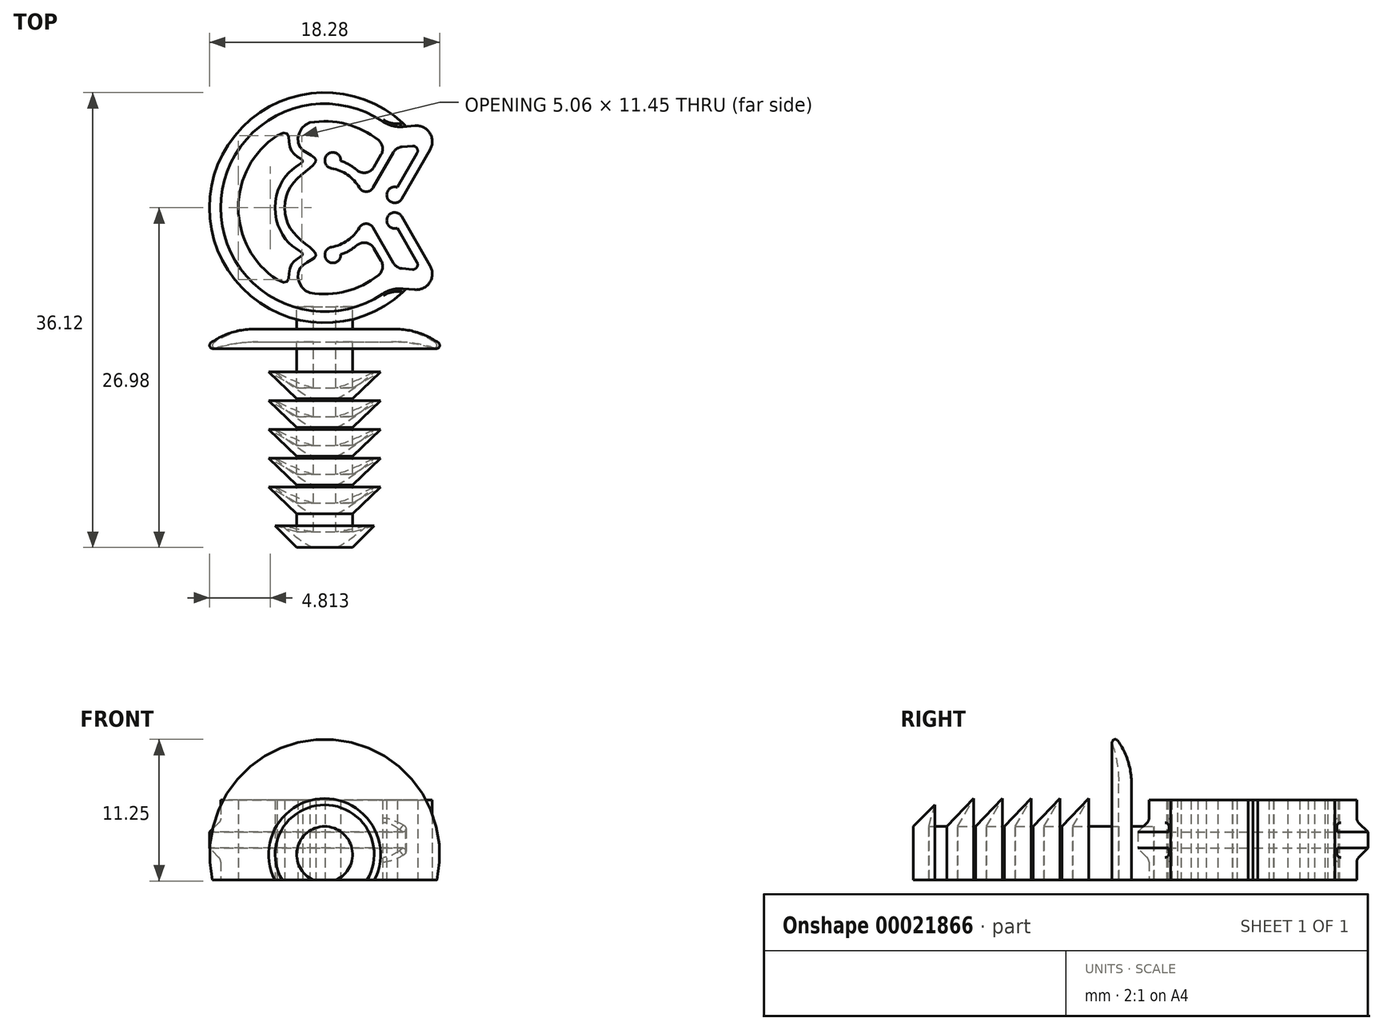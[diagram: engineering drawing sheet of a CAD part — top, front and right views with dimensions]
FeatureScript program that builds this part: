
annotation { "Feature Type Name" : "Feature", "Feature Type Description" : "" }
export const myFeature = defineFeature(function(context is Context, id is Id, definition is map)
    precondition{}
    {
        {
            var Q0;
            Q0=qCreatedBy(makeId("Top.planeOp"),FACE);
            var sketch = newSketch(context, id + "F0", { "sketchPlane" : qUnion([Q0])});
            skLineSegment(sketch, "E0", {"start": v(0, 0) * mm, "end": v(27.93, 0) * mm, "construction": true});
            skLineSegment(sketch, "E1", {"start": v(6.24, 6.43) * mm, "end": v(7.17, 6.52) * mm});
            skLineSegment(sketch, "E2", {"start": v(8.38, 4.62) * mm, "end": v(6.12, 0.7) * mm});
            skLineSegment(sketch, "E3", {"start": v(5.77, 1.62) * mm, "end": v(7.34, 4.34) * mm});
            skLineSegment(sketch, "E4", {"start": v(6.98, 4.9) * mm, "end": v(6.16, 4.83) * mm});
            skArc(sketch, "E5", {"start": v(5.77, 1.62) * mm, "mid": v(4.98, 0.8) * mm, "end": v(6.12, 0.7) * mm});
            skPoint(sketch, "E6.visualSharp", {"position": v(9.6, 6.73) * mm});
            skArc(sketch, "E6.filletArc", {"start": v(8.38, 4.62) * mm, "mid": v(8.35, 5.93) * mm, "end": v(7.17, 6.52) * mm});
            skPoint(sketch, "E7.visualSharp", {"position": v(7.7, 4.97) * mm});
            skArc(sketch, "E7.filletArc", {"start": v(7.34, 4.34) * mm, "mid": v(7.33, 4.73) * mm, "end": v(6.98, 4.9) * mm});
            skArc(sketch, "E8", {"start": v(4.6, 6.86) * mm, "mid": v(-3.88, 7.28) * mm, "end": v(-8.26, 0) * mm});
            skArc(sketch, "E9", {"start": v(4.28, 5.36) * mm, "mid": v(1.7, 6.64) * mm, "end": v(-1.17, 6.76) * mm});
            skLineSegment(sketch, "E10", {"start": v(0, 0) * mm, "end": v(-13.62, 0) * mm, "construction": true});
            skPoint(sketch, "E11.visualSharp", {"position": v(5.27, 6.35) * mm});
            skArc(sketch, "E11.filletArc", {"start": v(4.6, 6.86) * mm, "mid": v(5.38, 6.5) * mm, "end": v(6.24, 6.43) * mm});
            skLineSegment(sketch, "E12", {"start": v(5.47, 4.4) * mm, "end": v(3.85, 1.59) * mm});
            skLineSegment(sketch, "E13", {"start": v(4.5, 4.22) * mm, "end": v(3.91, 3.22) * mm});
            skPoint(sketch, "E14", {"position": v(-0.35, 3.16) * mm});
            skArc(sketch, "E15", {"start": v(2.75, 1.59) * mm, "mid": v(1.82, 2.6) * mm, "end": v(0.54, 3.13) * mm});
            skPoint(sketch, "E16", {"position": v(0.3, 3.88) * mm});
            skPoint(sketch, "E17.visualSharp", {"position": v(3.15, 0.38) * mm});
            skArc(sketch, "E17.filletArc", {"start": v(2.75, 1.59) * mm, "mid": v(3.3, 1.27) * mm, "end": v(3.85, 1.59) * mm});
            skArc(sketch, "E18", {"start": v(1.29, 3.72) * mm, "mid": v(0.26, 4.25) * mm, "end": v(0.54, 3.13) * mm});
            skPoint(sketch, "E19.visualSharp", {"position": v(4.85, 4.85) * mm});
            skArc(sketch, "E19.filletArc", {"start": v(4.5, 4.22) * mm, "mid": v(4.6, 4.83) * mm, "end": v(4.28, 5.36) * mm});
            skPoint(sketch, "E20.visualSharp", {"position": v(5.7, 4.8) * mm});
            skArc(sketch, "E20.filletArc", {"start": v(6.16, 4.83) * mm, "mid": v(5.76, 4.7) * mm, "end": v(5.47, 4.4) * mm});
            skCircle(sketch, "E21", {"center": v(0, 0) * mm, "radius": 3.18 * mm, "construction": true});
            skArc(sketch, "E22", {"start": v(2.56, 2.99) * mm, "mid": v(1.96, 3.42) * mm, "end": v(1.29, 3.72) * mm});
            skLineSegment(sketch, "E23", {"start": v(0, 0) * mm, "end": v(1.94, 4.22) * mm, "construction": true});
            skPoint(sketch, "E24", {"position": v(1.64, 3.58) * mm});
            skPoint(sketch, "E25", {"position": v(1.33, 2.89) * mm});
            skPoint(sketch, "E26.visualSharp", {"position": v(3.3, 2.15) * mm});
            skArc(sketch, "E26.filletArc", {"start": v(2.56, 2.99) * mm, "mid": v(3.3, 2.79) * mm, "end": v(3.91, 3.22) * mm});
            skFitSpline(sketch, "E27", {"points": [v(-1.17, 6.76) * mm, v(-2.03, 4.92) * mm, v(-0.7, 3.83) * mm, v(-2, 2.46) * mm, v(-3.18, 0) * mm], "startDerivative": vector(-8.5, -2.05) * mm, "endDerivative": vector(0.11, -11.22) * mm});
            skFitSpline(sketch, "E28", {"points": [v(-3.78, 5.72) * mm, v(-2.74, 4.77) * mm, v(-1.76, 3.72) * mm, v(-2.58, 3.03) * mm, v(-3.94, 0) * mm], "startDerivative": vector(15.56, 9.08) * mm, "endDerivative": vector(0.12, -11.3) * mm});
            skArc(sketch, "E29.trimOffspring", {"start": v(-3.78, 5.72) * mm, "mid": v(-6.04, 3.25) * mm, "end": v(-6.86, 0) * mm});
            skArc(sketch, "E30.MirrorCS", {"start": v(6.16, -4.83) * mm, "mid": v(5.76, -4.7) * mm, "end": v(5.47, -4.4) * mm});
            skArc(sketch, "E31.MirrorCS", {"start": v(4.5, -4.22) * mm, "mid": v(4.6, -4.83) * mm, "end": v(4.28, -5.36) * mm});
            skPoint(sketch, "E32.MirrorP", {"position": v(5.7, -4.8) * mm});
            skArc(sketch, "E33.MirrorCS", {"start": v(2.56, -2.99) * mm, "mid": v(1.96, -3.42) * mm, "end": v(1.29, -3.72) * mm});
            skArc(sketch, "E34.MirrorCS", {"start": v(2.56, -2.99) * mm, "mid": v(3.3, -2.79) * mm, "end": v(3.91, -3.22) * mm});
            skFitSpline(sketch, "E35.MirrorCS", {"points": [v(-1.17, -6.76) * mm, v(-2.03, -4.92) * mm, v(-0.7, -3.83) * mm, v(-2, -2.46) * mm, v(-3.18, 0) * mm], "startDerivative": vector(-8.5, 2.05) * mm, "endDerivative": vector(0.11, 11.22) * mm});
            skArc(sketch, "E36.MirrorCS", {"start": v(-3.78, -5.72) * mm, "mid": v(-6.04, -3.25) * mm, "end": v(-6.86, 0) * mm});
            skFitSpline(sketch, "E37.MirrorCS", {"points": [v(-3.78, -5.72) * mm, v(-2.74, -4.77) * mm, v(-1.76, -3.72) * mm, v(-2.58, -3.03) * mm, v(-3.94, 0) * mm], "startDerivative": vector(15.56, -9.08) * mm, "endDerivative": vector(0.12, 11.3) * mm});
            skPoint(sketch, "E38.MirrorP", {"position": v(4.85, -4.85) * mm});
            skLineSegment(sketch, "E39.MirrorCS", {"start": v(4.5, -4.22) * mm, "end": v(3.91, -3.22) * mm});
            skLineSegment(sketch, "E40.MirrorCS", {"start": v(5.77, -1.62) * mm, "end": v(7.34, -4.34) * mm});
            skPoint(sketch, "E41.MirrorP", {"position": v(0.3, -3.88) * mm});
            skArc(sketch, "E42.MirrorCS", {"start": v(5.77, -1.62) * mm, "mid": v(4.98, -0.8) * mm, "end": v(6.12, -0.7) * mm});
            skArc(sketch, "E43.MirrorCS", {"start": v(2.75, -1.59) * mm, "mid": v(1.82, -2.6) * mm, "end": v(0.54, -3.13) * mm});
            skLineSegment(sketch, "E44.MirrorCS", {"start": v(6.98, -4.9) * mm, "end": v(6.16, -4.83) * mm});
            skLineSegment(sketch, "E45.MirrorCS", {"start": v(8.38, -4.62) * mm, "end": v(6.12, -0.7) * mm});
            skPoint(sketch, "E46.MirrorP", {"position": v(1.64, -3.58) * mm});
            skLineSegment(sketch, "E47.MirrorCS", {"start": v(6.24, -6.43) * mm, "end": v(7.17, -6.52) * mm});
            skLineSegment(sketch, "E48.MirrorCS", {"start": v(5.47, -4.4) * mm, "end": v(3.85, -1.59) * mm});
            skArc(sketch, "E49.MirrorCS", {"start": v(4.6, -6.86) * mm, "mid": v(5.38, -6.5) * mm, "end": v(6.24, -6.43) * mm});
            skPoint(sketch, "E50.MirrorP", {"position": v(1.33, -2.89) * mm});
            skArc(sketch, "E51.MirrorCS", {"start": v(2.75, -1.59) * mm, "mid": v(3.3, -1.27) * mm, "end": v(3.85, -1.59) * mm});
            skPoint(sketch, "E52.MirrorP", {"position": v(-0.35, -3.16) * mm});
            skPoint(sketch, "E53.MirrorP", {"position": v(5.27, -6.35) * mm});
            skArc(sketch, "E54.MirrorCS", {"start": v(4.28, -5.36) * mm, "mid": v(1.7, -6.64) * mm, "end": v(-1.17, -6.76) * mm});
            skPoint(sketch, "E55.MirrorP", {"position": v(3.15, -0.38) * mm});
            skArc(sketch, "E56.MirrorCS", {"start": v(8.38, -4.62) * mm, "mid": v(8.35, -5.93) * mm, "end": v(7.17, -6.52) * mm});
            skArc(sketch, "E57.MirrorCS", {"start": v(4.6, -6.86) * mm, "mid": v(-3.88, -7.28) * mm, "end": v(-8.26, 0) * mm});
            skPoint(sketch, "E58.MirrorP", {"position": v(3.3, -2.15) * mm});
            skPoint(sketch, "E59.MirrorP", {"position": v(7.7, -4.97) * mm});
            skArc(sketch, "E60.MirrorCS", {"start": v(1.29, -3.72) * mm, "mid": v(0.26, -4.25) * mm, "end": v(0.54, -3.13) * mm});
            skArc(sketch, "E61.MirrorCS", {"start": v(7.34, -4.34) * mm, "mid": v(7.33, -4.73) * mm, "end": v(6.98, -4.9) * mm});
            skSolve(sketch);
        }
        {
            var Q0;
            Q0=makeQuery(id+"F0.imprint","IMPRINT",FACE,{"disambiguationData":[TD([[makeQuery(id+"F0.imprint","IMPRINT",EDGE,{"derivedFrom":sQuery(id+"F0.wireOp",EDGE,"E1")}),-1.0]])]});
            extrude(context, id + "F1", {"entities" : qUnion([Q0]), "endBound" : BoundingType.SYMMETRIC, "depth" : 6.35 * mm});
        }
        {
            var Q0;
            Q0=qCreatedBy(makeId("Right.planeOp"),FACE);
            var sketch = newSketch(context, id + "F2", { "sketchPlane" : qUnion([Q0])});
            skLineSegment(sketch, "E62", {"start": v(-9.14, 0.64) * mm, "end": v(-9.14, -0.64) * mm});
            skLineSegment(sketch, "E63", {"start": v(-9.14, -0.64) * mm, "end": v(-7.96, -1.82) * mm});
            skLineSegment(sketch, "E64", {"start": v(-7.96, -1.82) * mm, "end": v(-7.96, 1.82) * mm});
            skLineSegment(sketch, "E65", {"start": v(-7.96, 1.82) * mm, "end": v(-9.14, 0.64) * mm});
            skPoint(sketch, "E66", {"position": v(-9.14, 0) * mm});
            skPoint(sketch, "E67", {"position": v(-8.26, 0) * mm});
            skLineSegment(sketch, "E68", {"start": v(0, 0) * mm, "end": v(0, 5.93) * mm, "construction": true});
            skSolve(sketch);
        }
        {
            var Q0;
            Q0=makeQuery(id+"F2.imprint","IMPRINT",FACE,{"disambiguationData":[TD([[makeQuery(id+"F2.imprint","IMPRINT",EDGE,{"derivedFrom":sQuery(id+"F2.wireOp",EDGE,"E62")}),1.0]])]});
            var Q1;
            Q1=sQuery(id+"F2.wireOp",EDGE,"E68");
            revolve(context, id + "F3", {"operationType" : NewBodyOperationType.ADD, "entities" : qUnion([Q0]), "axis" : qUnion([Q1]), "revolveType" : RevolveType.TWO_DIRECTIONS, "angle" : 45 * degree, "angleBack" : 135 * degree});
        }
        {
            var Q0;
            Q0=makeQuery(id+"F3.boolean.opBoolean","INTERSECT",EDGE,{"derivedFrom":[makeQuery(id+"F1.opExtrude","SWEPT_FACE",FACE,{"disambiguationData":[OSD([sQuery(id+"F0.wireOp",EDGE,"E8"),sQuery(id+"F0.wireOp",EDGE,"E57.MirrorCS")])]}),makeQuery(id+"F3.opRevolve","SWEPT_FACE",FACE,{"disambiguationData":[OSD([sQuery(id+"F2.wireOp",EDGE,"E63")])]})]});
            var Q1;
            Q1=makeQuery(id+"F3.boolean.opBoolean","INTERSECT",EDGE,{"derivedFrom":[makeQuery(id+"F1.opExtrude","SWEPT_FACE",FACE,{"disambiguationData":[OSD([sQuery(id+"F0.wireOp",EDGE,"E8"),sQuery(id+"F0.wireOp",EDGE,"E57.MirrorCS")])]}),makeQuery(id+"F3.opRevolve","SWEPT_FACE",FACE,{"disambiguationData":[OSD([sQuery(id+"F2.wireOp",EDGE,"E65")])]})]});
            var Q2;
            Q2=makeQuery(id+"F3.boolean.opBoolean","INTERSECT",EDGE,{"derivedFrom":[makeQuery(id+"F1.opExtrude","SWEPT_FACE",FACE,{"disambiguationData":[OSD([sQuery(id+"F0.wireOp",EDGE,"E1")])]}),makeQuery(id+"F3.opRevolve","SWEPT_FACE",FACE,{"disambiguationData":[OSD([sQuery(id+"F2.wireOp",EDGE,"E65")])]})]});
            fillet(context, id + "F4", {"entities" : qUnion([Q0, Q1, Q2]), "radius" : 0.5 * mm, "tangentPropagation" : true, "allowEdgeOverflow" : false});
        }
        {
            var Q0;
            Q0=qCreatedBy(makeId("Right.planeOp"),FACE);
            var sketch = newSketch(context, id + "F5", { "sketchPlane" : qUnion([Q0])});
            skLineSegment(sketch, "E69", {"start": v(-7.87, 1.08) * mm, "end": v(-9.65, 1.08) * mm});
            skLineSegment(sketch, "E70", {"start": v(-10.67, 4.53) * mm, "end": v(-10.67, 1.08) * mm});
            skLineSegment(sketch, "E71", {"start": v(-10.67, 1.08) * mm, "end": v(-14.31, 1.08) * mm});
            skLineSegment(sketch, "E72", {"start": v(-14.31, 1.08) * mm, "end": v(-13.03, 3.3) * mm});
            skLineSegment(sketch, "E73", {"start": v(-13.03, 3.3) * mm, "end": v(-15.18, 1.08) * mm});
            skLineSegment(sketch, "E74", {"start": v(-9.65, 1.08) * mm, "end": v(-9.65, 4.53) * mm});
            skArc(sketch, "E75", {"start": v(-9.65, 4.53) * mm, "mid": v(-9.93, 6.3) * mm, "end": v(-10.73, 7.9) * mm});
            skArc(sketch, "E76", {"start": v(-10.67, 4.53) * mm, "mid": v(-10.8, 6.12) * mm, "end": v(-11.18, 7.67) * mm});
            skLineSegment(sketch, "E77", {"start": v(0.86, -1.14) * mm, "end": v(-26.5, -1.14) * mm, "construction": true});
            skLineSegment(sketch, "E78", {"start": v(-15.18, 1.08) * mm, "end": v(-16.6, 1.08) * mm});
            skLineSegment(sketch, "E79.1.0.0", {"start": v(-15.32, 3.3) * mm, "end": v(-17.46, 1.08) * mm});
            skLineSegment(sketch, "E79.1.0.1", {"start": v(-17.46, 1.08) * mm, "end": v(-18.88, 1.08) * mm});
            skLineSegment(sketch, "E79.1.0.2", {"start": v(-16.6, 1.08) * mm, "end": v(-15.32, 3.3) * mm});
            skLineSegment(sketch, "E79.2.0.0", {"start": v(-17.6, 3.3) * mm, "end": v(-19.75, 1.08) * mm});
            skLineSegment(sketch, "E79.2.0.1", {"start": v(-19.75, 1.08) * mm, "end": v(-21.17, 1.08) * mm});
            skLineSegment(sketch, "E79.2.0.2", {"start": v(-18.88, 1.08) * mm, "end": v(-17.6, 3.3) * mm});
            skLineSegment(sketch, "E79.direction1", {"start": v(-15.18, 1.08) * mm, "end": v(-17.46, 1.08) * mm, "construction": true});
            skLineSegment(sketch, "E80.0.3.0", {"start": v(-19.89, 3.3) * mm, "end": v(-22.03, 1.08) * mm});
            skLineSegment(sketch, "E80.3.3.0", {"start": v(-22.03, 1.08) * mm, "end": v(-23.46, 1.08) * mm});
            skLineSegment(sketch, "E80.6.3.0", {"start": v(-21.17, 1.08) * mm, "end": v(-19.89, 3.3) * mm});
            skLineSegment(sketch, "E80.0.4.0", {"start": v(-22.17, 3.3) * mm, "end": v(-24.32, 1.08) * mm});
            skLineSegment(sketch, "E80.3.4.0", {"start": v(-24.32, 1.08) * mm, "end": v(-25.74, 1.08) * mm});
            skLineSegment(sketch, "E80.6.4.0", {"start": v(-23.46, 1.08) * mm, "end": v(-22.17, 3.3) * mm});
            skLineSegment(sketch, "E81", {"start": v(-25.74, 1.08) * mm, "end": v(-25.74, 1.08) * mm});
            skLineSegment(sketch, "E82", {"start": v(-25.74, 1.08) * mm, "end": v(-25.26, 2.8) * mm});
            skLineSegment(sketch, "E83", {"start": v(-25.26, 2.8) * mm, "end": v(-26.98, 1.08) * mm});
            skLineSegment(sketch, "E84", {"start": v(-26.98, 1.08) * mm, "end": v(-26.98, -1.14) * mm});
            skLineSegment(sketch, "E85", {"start": v(-26.98, -1.14) * mm, "end": v(-7.87, -1.14) * mm});
            skLineSegment(sketch, "E86", {"start": v(-7.87, 1.08) * mm, "end": v(-7.87, -1.14) * mm});
            skArc(sketch, "E87", {"start": v(-11.18, 7.67) * mm, "mid": v(-11.05, 7.97) * mm, "end": v(-10.73, 7.9) * mm});
            skLineSegment(sketch, "E88", {"start": v(-10.67, 4.53) * mm, "end": v(-9.65, 4.53) * mm, "construction": true});
            skSolve(sketch);
        }
        {
            var Q0;
            Q0 = qSketchRegion(id + "F5", true);
            var Q1;
            Q1=sQuery(id+"F5.wireOp",EDGE,"E77");
            revolve(context, id + "F6", {"entities" : qUnion([Q0]), "axis" : qUnion([Q1]), "revolveType" : RevolveType.FULL});
        }
        {
            var Q0;
            Q0=makeQuery(id+"F1.opExtrude","CAP_FACE",FACE,{"disambiguationData":[OSD([sQuery(id+"F0.wireOp",EDGE,"E1"),sQuery(id+"F0.wireOp",EDGE,"E2"),sQuery(id+"F0.wireOp",EDGE,"E3"),sQuery(id+"F0.wireOp",EDGE,"E4"),sQuery(id+"F0.wireOp",EDGE,"E5"),sQuery(id+"F0.wireOp",EDGE,"E6.filletArc"),sQuery(id+"F0.wireOp",EDGE,"E7.filletArc"),sQuery(id+"F0.wireOp",EDGE,"E8"),sQuery(id+"F0.wireOp",EDGE,"E9"),sQuery(id+"F0.wireOp",EDGE,"E11.filletArc"),sQuery(id+"F0.wireOp",EDGE,"E12"),sQuery(id+"F0.wireOp",EDGE,"E13"),sQuery(id+"F0.wireOp",EDGE,"E15"),sQuery(id+"F0.wireOp",EDGE,"E17.filletArc"),sQuery(id+"F0.wireOp",EDGE,"E18"),sQuery(id+"F0.wireOp",EDGE,"E19.filletArc"),sQuery(id+"F0.wireOp",EDGE,"E20.filletArc"),sQuery(id+"F0.wireOp",EDGE,"E22"),sQuery(id+"F0.wireOp",EDGE,"E26.filletArc"),sQuery(id+"F0.wireOp",EDGE,"E27"),sQuery(id+"F0.wireOp",EDGE,"E28"),sQuery(id+"F0.wireOp",EDGE,"E29.trimOffspring"),sQuery(id+"F0.wireOp",EDGE,"E30.MirrorCS"),sQuery(id+"F0.wireOp",EDGE,"E31.MirrorCS"),sQuery(id+"F0.wireOp",EDGE,"E33.MirrorCS"),sQuery(id+"F0.wireOp",EDGE,"E34.MirrorCS"),sQuery(id+"F0.wireOp",EDGE,"E35.MirrorCS"),sQuery(id+"F0.wireOp",EDGE,"E36.MirrorCS"),sQuery(id+"F0.wireOp",EDGE,"E37.MirrorCS"),sQuery(id+"F0.wireOp",EDGE,"E39.MirrorCS"),sQuery(id+"F0.wireOp",EDGE,"E40.MirrorCS"),sQuery(id+"F0.wireOp",EDGE,"E42.MirrorCS"),sQuery(id+"F0.wireOp",EDGE,"E43.MirrorCS"),sQuery(id+"F0.wireOp",EDGE,"E44.MirrorCS"),sQuery(id+"F0.wireOp",EDGE,"E45.MirrorCS"),sQuery(id+"F0.wireOp",EDGE,"E47.MirrorCS"),sQuery(id+"F0.wireOp",EDGE,"E48.MirrorCS"),sQuery(id+"F0.wireOp",EDGE,"E49.MirrorCS"),sQuery(id+"F0.wireOp",EDGE,"E51.MirrorCS"),sQuery(id+"F0.wireOp",EDGE,"E54.MirrorCS"),sQuery(id+"F0.wireOp",EDGE,"E56.MirrorCS"),sQuery(id+"F0.wireOp",EDGE,"E57.MirrorCS"),sQuery(id+"F0.wireOp",EDGE,"E60.MirrorCS"),sQuery(id+"F0.wireOp",EDGE,"E61.MirrorCS")])],"isStart":true});
            var sketch = newSketch(context, id + "F7", { "sketchPlane" : qUnion([Q0])});
            skLineSegment(sketch, "E89.bottom", {"start": v(-15.14, 4.57) * mm, "end": v(15.97, 4.57) * mm});
            skLineSegment(sketch, "E89.top", {"start": v(-15.14, 29.73) * mm, "end": v(15.97, 29.73) * mm});
            skLineSegment(sketch, "E89.left", {"start": v(-15.14, 4.57) * mm, "end": v(-15.14, 29.73) * mm});
            skLineSegment(sketch, "E89.right", {"start": v(15.97, 4.57) * mm, "end": v(15.97, 29.73) * mm});
            skSolve(sketch);
        }
        {
            var Q0;
            Q0 = qSketchRegion(id + "F7", true);
            extrude(context, id + "F8", {"entities" : qUnion([Q0]), "operationType" : NewBodyOperationType.REMOVE, "depth" : 25.4 * mm});
        }
    });
